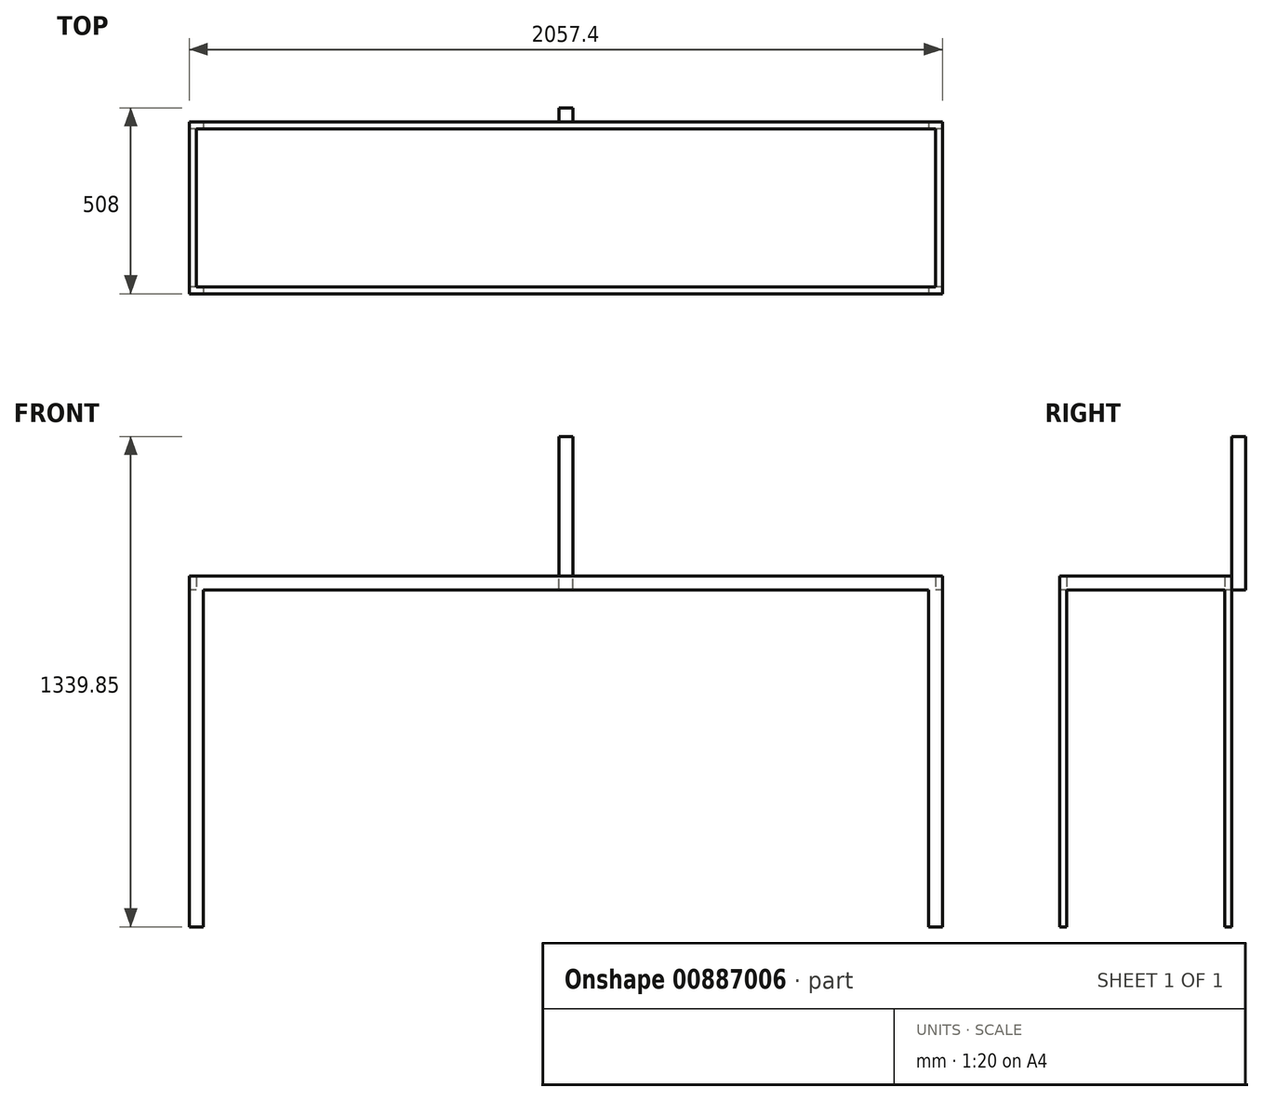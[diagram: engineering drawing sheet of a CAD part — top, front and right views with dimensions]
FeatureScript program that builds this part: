
annotation { "Feature Type Name" : "Feature", "Feature Type Description" : "" }
export const myFeature = defineFeature(function(context is Context, id is Id, definition is map)
    precondition{}
    {
        {
            var Q0;
            Q0=qCreatedBy(makeId("Top.planeOp"),FACE);
            var sketch = newSketch(context, id + "F0", { "sketchPlane" : qUnion([Q0])});
            skLineSegment(sketch, "E0.bottom", {"start": v(-1028.7, 234.95) * mm, "end": v(1028.7, 234.95) * mm});
            skLineSegment(sketch, "E0.top", {"start": v(-1028.7, -234.95) * mm, "end": v(1028.7, -234.95) * mm});
            skLineSegment(sketch, "E0.left", {"start": v(-1028.7, 234.95) * mm, "end": v(-1028.7, -234.95) * mm});
            skLineSegment(sketch, "E0.right", {"start": v(1028.7, 234.95) * mm, "end": v(1028.7, -234.95) * mm});
            skPoint(sketch, "E0.middle", {"position": v(0, 0) * mm});
            skLineSegment(sketch, "E1.bottom", {"start": v(-1009.65, 215.9) * mm, "end": v(1009.65, 215.9) * mm});
            skLineSegment(sketch, "E1.top", {"start": v(-1009.65, -215.9) * mm, "end": v(1009.65, -215.9) * mm});
            skLineSegment(sketch, "E1.left", {"start": v(-1009.65, 215.9) * mm, "end": v(-1009.65, -215.9) * mm});
            skLineSegment(sketch, "E1.right", {"start": v(1009.65, 215.9) * mm, "end": v(1009.65, -215.9) * mm});
            skSolve(sketch);
        }
        {
            var Q0;
            Q0 = qSketchRegion(id + "F0", true);
            extrude(context, id + "F1", {"entities" : qUnion([Q0]), "endBound" : BoundingType.SYMMETRIC, "depth" : 958.85 * mm, "offsetDistance" : 25.4 * mm});
        }
        {
            var Q0;
            Q0=makeQuery(id+"F1.opExtrude","SWEPT_FACE",FACE,{"disambiguationData":[OSD([sQuery(id+"F0.wireOp",EDGE,"E0.top")])]});
            var sketch = newSketch(context, id + "F2", { "sketchPlane" : qUnion([Q0])});
            skLineSegment(sketch, "E2.bottom", {"start": v(-990.6, -479.43) * mm, "end": v(990.6, -479.43) * mm});
            skLineSegment(sketch, "E2.top", {"start": v(-990.6, 441.33) * mm, "end": v(990.6, 441.33) * mm});
            skLineSegment(sketch, "E2.left", {"start": v(-990.6, -479.43) * mm, "end": v(-990.6, 441.33) * mm});
            skLineSegment(sketch, "E2.right", {"start": v(990.6, -479.43) * mm, "end": v(990.6, 441.33) * mm});
            skPoint(sketch, "E3", {"position": v(0, 441.33) * mm});
            skSolve(sketch);
        }
        {
            var Q0;
            Q0=makeQuery(id+"F2.imprint","IMPRINT",FACE,{"disambiguationData":[TD([[makeQuery(id+"F2.imprint","IMPRINT",EDGE,{"derivedFrom":sQuery(id+"F2.wireOp",EDGE,"E2.bottom")}),1.0]])]});
            extrude(context, id + "F3", {"entities" : qUnion([Q0]), "operationType" : NewBodyOperationType.REMOVE, "endBound" : BoundingType.THROUGH_ALL, "oppositeDirection" : true, "depth" : 25.4 * mm, "offsetDistance" : 25.4 * mm});
        }
        {
            var Q0;
            Q0=makeQuery(id+"F1.opExtrude","SWEPT_FACE",FACE,{"disambiguationData":[OSD([sQuery(id+"F0.wireOp",EDGE,"E0.left")])]});
            var sketch = newSketch(context, id + "F4", { "sketchPlane" : qUnion([Q0])});
            skLineSegment(sketch, "E4.bottom", {"start": v(-215.9, -479.43) * mm, "end": v(215.9, -479.43) * mm});
            skLineSegment(sketch, "E4.top", {"start": v(-215.9, 441.33) * mm, "end": v(215.9, 441.33) * mm});
            skLineSegment(sketch, "E4.left", {"start": v(-215.9, -479.43) * mm, "end": v(-215.9, 441.33) * mm});
            skLineSegment(sketch, "E4.right", {"start": v(215.9, -479.43) * mm, "end": v(215.9, 441.33) * mm});
            skPoint(sketch, "E5", {"position": v(0, 441.33) * mm});
            skSolve(sketch);
        }
        {
            var Q0;
            Q0 = qSketchRegion(id + "F4", true);
            extrude(context, id + "F5", {"entities" : qUnion([Q0]), "operationType" : NewBodyOperationType.REMOVE, "endBound" : BoundingType.THROUGH_ALL, "oppositeDirection" : true, "depth" : 25.4 * mm, "offsetDistance" : 25.4 * mm});
        }
        {
            var Q0;
            Q0=makeQuery(id+"F1.opExtrude","SWEPT_FACE",FACE,{"disambiguationData":[OSD([sQuery(id+"F0.wireOp",EDGE,"E0.bottom")])]});
            var sketch = newSketch(context, id + "F6", { "sketchPlane" : qUnion([Q0])});
            skLineSegment(sketch, "E6.bottom", {"start": v(-19.05, 441.33) * mm, "end": v(19.05, 441.33) * mm});
            skLineSegment(sketch, "E6.top", {"start": v(-19.05, 479.43) * mm, "end": v(19.05, 479.43) * mm});
            skLineSegment(sketch, "E6.left", {"start": v(-19.05, 441.33) * mm, "end": v(-19.05, 479.43) * mm});
            skLineSegment(sketch, "E6.right", {"start": v(19.05, 441.33) * mm, "end": v(19.05, 479.43) * mm});
            skPoint(sketch, "E7", {"position": v(0, 479.43) * mm});
            skSolve(sketch);
        }
        {
            var Q0;
            Q0 = qSketchRegion(id + "F6", true);
            extrude(context, id + "F7", {"entities" : qUnion([Q0]), "operationType" : NewBodyOperationType.ADD, "depth" : 38.1 * mm, "offsetDistance" : 25.4 * mm});
        }
        {
            var Q0;
            Q0=makeQuery(id+"F7.boolean.opBoolean","MERGE",FACE,{"derivedFrom":[makeQuery(id+"F1.opExtrude","CAP_FACE",FACE,{"disambiguationData":[OSD([sQuery(id+"F0.wireOp",EDGE,"E0.bottom"),sQuery(id+"F0.wireOp",EDGE,"E0.top"),sQuery(id+"F0.wireOp",EDGE,"E0.left"),sQuery(id+"F0.wireOp",EDGE,"E0.right"),sQuery(id+"F0.wireOp",EDGE,"E1.bottom"),sQuery(id+"F0.wireOp",EDGE,"E1.top"),sQuery(id+"F0.wireOp",EDGE,"E1.left"),sQuery(id+"F0.wireOp",EDGE,"E1.right")])],"isStart":false}),makeQuery(id+"F7.opExtrude","SWEPT_FACE",FACE,{"disambiguationData":[OSD([sQuery(id+"F6.wireOp",EDGE,"E6.top")])]})]});
            var sketch = newSketch(context, id + "F8", { "sketchPlane" : qUnion([Q0])});
            skLineSegment(sketch, "E8.bottom", {"start": v(-19.05, 273.05) * mm, "end": v(19.05, 273.05) * mm});
            skLineSegment(sketch, "E8.top", {"start": v(-19.05, 234.95) * mm, "end": v(19.05, 234.95) * mm});
            skLineSegment(sketch, "E8.left", {"start": v(-19.05, 273.05) * mm, "end": v(-19.05, 234.95) * mm});
            skLineSegment(sketch, "E8.right", {"start": v(19.05, 273.05) * mm, "end": v(19.05, 234.95) * mm});
            skPoint(sketch, "E8.middle", {"position": v(0, 254) * mm});
            skPoint(sketch, "E8.middle.positionSnap0", {"position": v(-19.05, 254) * mm});
            skPoint(sketch, "E8.middle.positionSnap1", {"position": v(0, 273.05) * mm});
            skPoint(sketch, "E8.centerSnap0", {"position": v(-19.05, 254) * mm});
            skPoint(sketch, "E8.centerSnap1", {"position": v(0, 273.05) * mm});
            skSolve(sketch);
        }
        {
            var Q0;
            Q0 = qSketchRegion(id + "F8", true);
            extrude(context, id + "F9", {"entities" : qUnion([Q0]), "operationType" : NewBodyOperationType.ADD, "depth" : 381 * mm, "offsetDistance" : 25.4 * mm});
        }
    });
